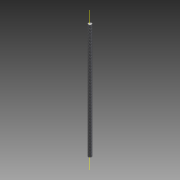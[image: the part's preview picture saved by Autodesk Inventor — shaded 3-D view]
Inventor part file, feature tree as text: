
AUTODESK INVENTOR PART (.ipt)
format: ipt  version: 2013 (Build 170138000, 138)  size: 67,584 bytes
history: native  units: in
note: dims shown in document units (in); Inventor stores cm internally (conversion verified against a paired STEP export)
features: extrude x1, thread x1, other x1, sketch x1
ambient origin geometry x8: Origin, YZ Plane, XZ Plane, XY Plane, X Axis, Y Axis, Z Axis, Center Point
bodies: Solid1 (feature_tree)
feature tree (4):
  extrude  "Extrusion1"  Depth=18.0in TaperAngle=0.0deg
  thread  "Thread1"  [1 undecoded]
  other  "Work Axis1"
  sketch  "Sketch1"  dims[d0=0.5in d2=18.0in d3=0.0in d4=1.0in d5=0.0in]
note: 1 required parameter value undecoded (feature->parameter linkage not recoverable at this tier; creation-order binding heuristic only, values carry confidence <= 0.55)
